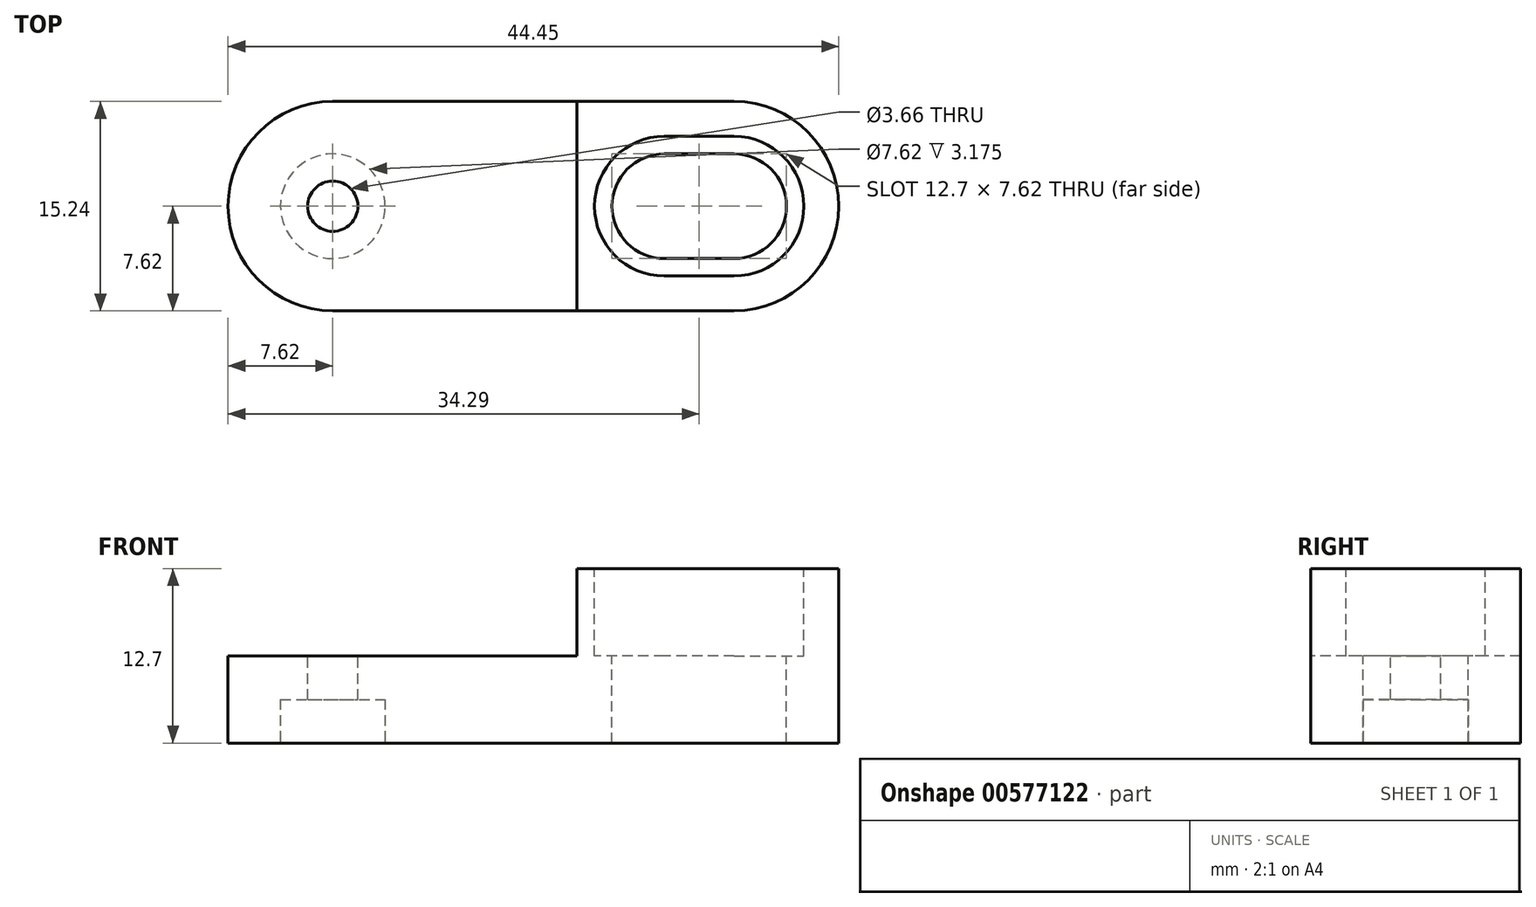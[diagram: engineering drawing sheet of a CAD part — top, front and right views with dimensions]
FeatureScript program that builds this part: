
annotation { "Feature Type Name" : "Feature", "Feature Type Description" : "" }
export const myFeature = defineFeature(function(context is Context, id is Id, definition is map)
    precondition{}
    {
        {
            var Q0;
            Q0=qCreatedBy(makeId("Top.planeOp"),FACE);
            var sketch = newSketch(context, id + "F0", { "sketchPlane" : qUnion([Q0])});
            skLineSegment(sketch, "E0.bottom", {"start": v(7.62, 0) * mm, "end": v(36.83, 0) * mm});
            skLineSegment(sketch, "E0.top", {"start": v(7.62, 15.24) * mm, "end": v(36.83, 15.24) * mm});
            skLineSegment(sketch, "E0.left", {"start": v(0, 7.62) * mm, "end": v(0, 7.62) * mm});
            skLineSegment(sketch, "E0.right", {"start": v(44.45, 7.62) * mm, "end": v(44.45, 7.62) * mm});
            skPoint(sketch, "E1.visualSharp", {"position": v(0, 15.24) * mm});
            skArc(sketch, "E1.filletArc", {"start": v(7.62, 15.24) * mm, "mid": v(2.23, 13) * mm, "end": v(0, 7.62) * mm});
            skPoint(sketch, "E2.visualSharp", {"position": v(0, 0) * mm});
            skArc(sketch, "E2.filletArc", {"start": v(0, 7.62) * mm, "mid": v(2.23, 2.23) * mm, "end": v(7.62, 0) * mm});
            skPoint(sketch, "E3.visualSharp", {"position": v(44.45, 15.24) * mm});
            skArc(sketch, "E3.filletArc", {"start": v(44.45, 7.62) * mm, "mid": v(42.22, 13) * mm, "end": v(36.83, 15.24) * mm});
            skPoint(sketch, "E4.visualSharp", {"position": v(44.45, 0) * mm});
            skArc(sketch, "E4.filletArc", {"start": v(36.83, 0) * mm, "mid": v(42.22, 2.23) * mm, "end": v(44.45, 7.62) * mm});
            skSolve(sketch);
        }
        {
            var Q0;
            Q0 = qSketchRegion(id + "F0", true);
            extrude(context, id + "F1", {"entities" : qUnion([Q0]), "depth" : 6.35 * mm, "offsetDistance" : 25.4 * mm});
        }
        {
            var Q0;
            Q0=makeQuery(id+"F1.opExtrude","CAP_FACE",FACE,{"disambiguationData":[OSD([sQuery(id+"F0.wireOp",EDGE,"E0.bottom"),sQuery(id+"F0.wireOp",EDGE,"E0.top"),sQuery(id+"F0.wireOp",EDGE,"E1.filletArc"),sQuery(id+"F0.wireOp",EDGE,"E2.filletArc"),sQuery(id+"F0.wireOp",EDGE,"E3.filletArc"),sQuery(id+"F0.wireOp",EDGE,"E4.filletArc")])],"isStart":false});
            var sketch = newSketch(context, id + "F2", { "sketchPlane" : qUnion([Q0])});
            skPoint(sketch, "E5", {"position": v(7.62, 7.62) * mm});
            skSolve(sketch);
        }
        {
            var Q0;
            Q0=sQuery(id+"F2.wireOp",VERTEX,"E5");
            var Q1;
            Q1=makeQuery(id+"F1.opExtrude","SWEPT_BODY",BODY,{"disambiguationData":[OSD([sQuery(id+"F0.wireOp",EDGE,"E0.bottom"),sQuery(id+"F0.wireOp",EDGE,"E0.top"),sQuery(id+"F0.wireOp",EDGE,"E1.filletArc"),sQuery(id+"F0.wireOp",EDGE,"E2.filletArc"),sQuery(id+"F0.wireOp",EDGE,"E3.filletArc"),sQuery(id+"F0.wireOp",EDGE,"E4.filletArc")])]});
            hole(context, id + "F3", {"style" : HoleStyle.SIMPLE, "endStyle" : HoleEndStyle.THROUGH, "standardTappedOrClearance" : lookupTablePath({ "standard" : "ANSI", "fit" : "Close", "size" : "#6", "type" : "Clearance" }), "standardBlindInLast" : lookupTablePath({ "fit" : "Close", "standard" : "ANSI", "size" : "#6", "type" : "Clearance" }), "holeDiameter" : 3.66 * mm, "majorDiameter" : 6.35 * mm, "isTappedThrough" : true, "tappedDepth" : 2.4 * mm, "tapClearance" : 3, "startFromSketch" : true, "locations" : qUnion([Q0]), "scope" : qUnion([Q1])});
        }
        {
            var Q0;
            Q0=makeQuery(id+"F1.opExtrude","CAP_FACE",FACE,{"disambiguationData":[OSD([sQuery(id+"F0.wireOp",EDGE,"E0.bottom"),sQuery(id+"F0.wireOp",EDGE,"E0.top"),sQuery(id+"F0.wireOp",EDGE,"E1.filletArc"),sQuery(id+"F0.wireOp",EDGE,"E2.filletArc"),sQuery(id+"F0.wireOp",EDGE,"E3.filletArc"),sQuery(id+"F0.wireOp",EDGE,"E4.filletArc")])],"isStart":false});
            var sketch = newSketch(context, id + "F4", { "sketchPlane" : qUnion([Q0])});
            skLineSegment(sketch, "E6", {"start": v(25.4, 15.24) * mm, "end": v(25.4, 0) * mm});
            skLineSegment(sketch, "E7", {"start": v(25.4, 15.24) * mm, "end": v(36.83, 15.24) * mm});
            skLineSegment(sketch, "E8", {"start": v(25.4, 0) * mm, "end": v(36.83, 0) * mm});
            skArc(sketch, "E9.0", {"start": v(36.83, 0) * mm, "mid": v(44.45, 7.62) * mm, "end": v(36.83, 15.24) * mm});
            skSolve(sketch);
        }
        {
            var Q0;
            Q0 = qSketchRegion(id + "F4", true);
            extrude(context, id + "F5", {"entities" : qUnion([Q0]), "operationType" : NewBodyOperationType.ADD, "depth" : 6.35 * mm, "offsetDistance" : 25.4 * mm});
        }
        {
            var Q0;
            Q0=makeQuery(id+"F5.opExtrude","CAP_FACE",FACE,{"disambiguationData":[OSD([sQuery(id+"F4.wireOp",EDGE,"E6"),sQuery(id+"F4.wireOp",EDGE,"E7"),sQuery(id+"F4.wireOp",EDGE,"E8"),sQuery(id+"F4.wireOp",EDGE,"E9.0")])],"isStart":false});
            var sketch = newSketch(context, id + "F6", { "sketchPlane" : qUnion([Q0])});
            skLineSegment(sketch, "E10", {"start": v(31.75, 7.62) * mm, "end": v(36.83, 7.62) * mm});
            skArc(sketch, "E11.0.startCap", {"start": v(31.75, 3.81) * mm, "mid": v(27.94, 7.62) * mm, "end": v(31.75, 11.43) * mm});
            skArc(sketch, "E11.0.endCap", {"start": v(36.83, 11.43) * mm, "mid": v(40.64, 7.62) * mm, "end": v(36.83, 3.81) * mm});
            skLineSegment(sketch, "E11.0.left", {"start": v(31.75, 11.43) * mm, "end": v(36.83, 11.43) * mm});
            skLineSegment(sketch, "E11.0.right", {"start": v(31.75, 3.81) * mm, "end": v(36.83, 3.81) * mm});
            skSolve(sketch);
        }
        {
            var Q0;
            Q0 = qSketchRegion(id + "F6", true);
            extrude(context, id + "F7", {"entities" : qUnion([Q0]), "operationType" : NewBodyOperationType.REMOVE, "endBound" : BoundingType.THROUGH_ALL, "oppositeDirection" : true, "depth" : 25.4 * mm, "offsetDistance" : 25.4 * mm});
        }
        {
            var Q0;
            Q0=makeQuery(id+"F5.opExtrude","CAP_FACE",FACE,{"disambiguationData":[OSD([sQuery(id+"F4.wireOp",EDGE,"E6"),sQuery(id+"F4.wireOp",EDGE,"E7"),sQuery(id+"F4.wireOp",EDGE,"E8"),sQuery(id+"F4.wireOp",EDGE,"E9.0")])],"isStart":false});
            var sketch = newSketch(context, id + "F8", { "sketchPlane" : qUnion([Q0])});
            skLineSegment(sketch, "E12", {"start": v(31.75, 7.62) * mm, "end": v(36.83, 7.62) * mm});
            skArc(sketch, "E13.0.startCap", {"start": v(31.75, 2.54) * mm, "mid": v(26.67, 7.62) * mm, "end": v(31.75, 12.7) * mm});
            skArc(sketch, "E13.0.endCap", {"start": v(36.83, 12.7) * mm, "mid": v(41.91, 7.62) * mm, "end": v(36.83, 2.54) * mm});
            skLineSegment(sketch, "E13.0.left", {"start": v(31.75, 12.7) * mm, "end": v(36.83, 12.7) * mm});
            skLineSegment(sketch, "E13.0.right", {"start": v(31.75, 2.54) * mm, "end": v(36.83, 2.54) * mm});
            skSolve(sketch);
        }
        {
            var Q0;
            Q0 = qSketchRegion(id + "F8", true);
            extrude(context, id + "F9", {"entities" : qUnion([Q0]), "operationType" : NewBodyOperationType.REMOVE, "oppositeDirection" : true, "depth" : 6.35 * mm, "offsetDistance" : 25.4 * mm});
        }
        {
            var Q0;
            Q0=makeQuery(id+"F1.opExtrude","CAP_FACE",FACE,{"disambiguationData":[OSD([sQuery(id+"F0.wireOp",EDGE,"E0.bottom"),sQuery(id+"F0.wireOp",EDGE,"E0.top"),sQuery(id+"F0.wireOp",EDGE,"E1.filletArc"),sQuery(id+"F0.wireOp",EDGE,"E2.filletArc"),sQuery(id+"F0.wireOp",EDGE,"E3.filletArc"),sQuery(id+"F0.wireOp",EDGE,"E4.filletArc")])],"isStart":true});
            var sketch = newSketch(context, id + "F10", { "sketchPlane" : qUnion([Q0])});
            skCircle(sketch, "E14", {"center": v(7.62, -7.62) * mm, "radius": 3.8 * mm});
            skSolve(sketch);
        }
        {
            var Q0;
            Q0 = qSketchRegion(id + "F10", true);
            extrude(context, id + "F11", {"entities" : qUnion([Q0]), "operationType" : NewBodyOperationType.REMOVE, "oppositeDirection" : true, "depth" : 3.17 * mm, "offsetDistance" : 25.4 * mm});
        }
    });
